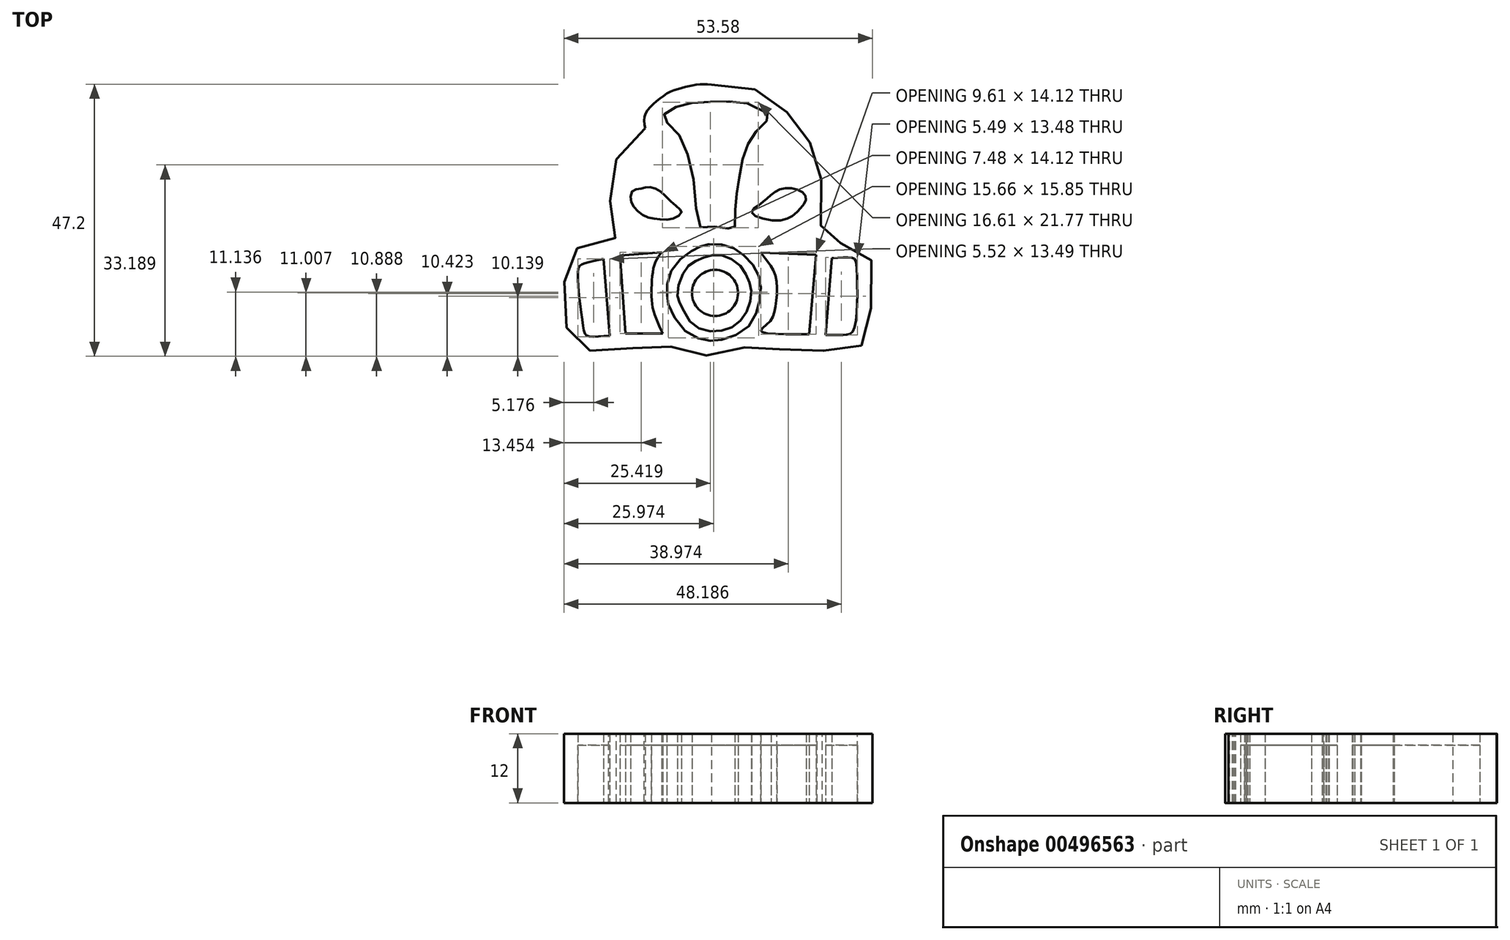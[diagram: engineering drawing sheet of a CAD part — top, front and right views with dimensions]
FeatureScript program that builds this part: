
annotation { "Feature Type Name" : "Feature", "Feature Type Description" : "" }
export const myFeature = defineFeature(function(context is Context, id is Id, definition is map)
    precondition{}
    {
        {
            var Q0;
            Q0=qCreatedBy(makeId("Top.planeOp"),FACE);
            var sketch = newSketch(context, id + "F0", { "sketchPlane" : qUnion([Q0])});
            skFitSpline(sketch, "E0", {"points": [v(28.28, 55.09) * mm, v(31.96, 54.97) * mm, v(34.93, 54.5) * mm, v(37.42, 53.55) * mm, v(40.27, 51.53) * mm, v(41.34, 50.34) * mm, v(41.93, 48.44) * mm, v(43.6, 47.61) * mm, v(45.85, 43.93) * mm, v(46.44, 42.39) * mm, v(47.15, 40.25) * mm, v(47.4, 36.22) * mm, v(47.5, 32.66) * mm, v(47.03, 29.8) * mm, v(46.68, 28.62) * mm, v(48.34, 27.9) * mm, v(51.9, 27.43) * mm, v(54.04, 26.72) * mm, v(55.7, 25.3) * mm, v(56.17, 23.28) * mm, v(56.17, 18.3) * mm, v(55.82, 15.2) * mm, v(55.46, 11.88) * mm, v(54.63, 10.22) * mm, v(52.97, 8.92) * mm, v(49.4, 8.56) * mm, v(47.63, 8.92) * mm, v(43.83, 9.04) * mm, v(40.62, 9.15) * mm, v(38.84, 9.27) * mm, v(35.4, 9.75) * mm, v(34.45, 9.75) * mm, v(32.9, 8.68) * mm, v(29.82, 7.97) * mm, v(27.33, 8.09) * mm, v(24.6, 8.8) * mm, v(23.06, 9.51) * mm, v(20.57, 9.51) * mm, v(18.55, 9.27) * mm, v(16.41, 9.27) * mm, v(13.2, 9.27) * mm, v(11.78, 8.8) * mm, v(7.27, 8.92) * mm, v(5.37, 9.4) * mm, v(3.71, 10.82) * mm, v(3.12, 13.43) * mm, v(3, 17.82) * mm, v(2.76, 20.43) * mm, v(2.76, 23.64) * mm, v(3.6, 25.53) * mm, v(5.37, 26.84) * mm, v(8.93, 27.43) * mm, v(11.19, 27.9) * mm, v(11.78, 29.45) * mm, v(11.43, 31.7) * mm, v(10.83, 34.2) * mm, v(10.48, 37.88) * mm, v(11.43, 40.85) * mm, v(12.02, 42.86) * mm, v(13.92, 45.83) * mm, v(16.77, 47.5) * mm], "startDerivative": vector(190.2, -1.39) * mm, "endDerivative": vector(161.55, 69.83) * mm});
            skFitSpline(sketch, "E1", {"points": [v(16.77, 47.5) * mm, v(16.77, 49.87) * mm, v(18.55, 52) * mm, v(21.04, 53.78) * mm, v(23.53, 54.61) * mm, v(25.79, 55.09) * mm, v(28.28, 55.09) * mm], "startDerivative": vector(-2.45, 15.47) * mm, "endDerivative": vector(15.57, -0.77) * mm});
            skFitSpline(sketch, "E2", {"points": [v(26.38, 30.28) * mm, v(25.43, 36.57) * mm, v(23.65, 44.29) * mm, v(21.4, 47.85) * mm, v(19.73, 49.4) * mm, v(20.68, 50.34) * mm, v(22.94, 51.53) * mm, v(26.62, 52) * mm, v(30.9, 52.12) * mm, v(35.05, 51.65) * mm, v(38.6, 49.4) * mm, v(37.42, 48.56) * mm, v(35.64, 46.3) * mm, v(34.33, 44.17) * mm, v(33.38, 40.6) * mm, v(32.8, 36.93) * mm, v(32.43, 34.32) * mm, v(32.32, 30.52) * mm, v(32.2, 30.04) * mm, v(30.9, 30.16) * mm, v(28.64, 30.4) * mm, v(26.38, 30.28) * mm]});
            skFitSpline(sketch, "E3", {"points": [v(16.05, 37.05) * mm, v(17.24, 37.29) * mm, v(19.02, 36.81) * mm, v(21.16, 34.91) * mm, v(22.82, 33.37) * mm, v(23.06, 32.9) * mm, v(21.63, 31.83) * mm, v(19.02, 31.7) * mm, v(16.89, 32.18) * mm, v(15.1, 33.49) * mm, v(14.27, 35.15) * mm, v(14.63, 36.7) * mm, v(16.05, 37.05) * mm]});
            skCircle(sketch, "E4", {"center": v(28.89, 18.92) * mm, "radius": 4 * mm});
            skPoint(sketch, "E4.first.point", {"position": v(26.38, 15.8) * mm});
            skPoint(sketch, "E4.second.point", {"position": v(31.49, 21.97) * mm});
            skPoint(sketch, "E4.third.point", {"position": v(32.43, 20.79) * mm});
            skFitSpline(sketch, "E5", {"points": [v(20.8, 16.99) * mm, v(20.57, 18.53) * mm, v(20.8, 21.62) * mm, v(23.41, 25.3) * mm, v(26.03, 26.84) * mm, v(27.45, 27.31) * mm, v(30.77, 27.2) * mm, v(33.5, 25.77) * mm, v(35.88, 23.16) * mm, v(36.83, 20.31) * mm, v(36.47, 16.87) * mm, v(34.57, 12.95) * mm, v(30.06, 10.82) * mm, v(27.45, 10.7) * mm, v(23.53, 12.48) * mm, v(20.8, 16.99) * mm]});
            skFitSpline(sketch, "E6", {"points": [v(23.3, 22.21) * mm, v(25.08, 24.23) * mm, v(27.33, 25.18) * mm, v(29.7, 25.53) * mm, v(32.9, 24) * mm, v(34.57, 21.5) * mm, v(35.16, 19.24) * mm, v(34.45, 15.8) * mm, v(32.2, 13.19) * mm, v(28.64, 12.24) * mm, v(24.96, 13.55) * mm, v(22.94, 16.87) * mm, v(22.35, 18.41) * mm, v(23.3, 22.21) * mm]});
            skFitSpline(sketch, "E7", {"points": [v(35.28, 32.9) * mm, v(36.7, 34.32) * mm, v(38.37, 35.74) * mm, v(40.27, 36.93) * mm, v(43, 36.93) * mm, v(44.66, 35.62) * mm, v(44.3, 34.32) * mm, v(42.64, 32.54) * mm, v(39.44, 31.47) * mm, v(35.28, 32.9) * mm]});
            skFitSpline(sketch, "E8", {"points": [v(46.44, 25.53) * mm, v(36.83, 25.9) * mm], "startDerivative": vector(-9.61, 0.36) * mm, "endDerivative": vector(-9.61, 0.36) * mm});
            skFitSpline(sketch, "E9", {"points": [v(36.83, 25.9) * mm, v(37.9, 24.58) * mm, v(39.44, 21.74) * mm, v(39.44, 16.99) * mm, v(38.37, 13.9) * mm, v(36.83, 12.36) * mm, v(45.25, 11.77) * mm], "startDerivative": vector(8.85, -10.47) * mm, "endDerivative": vector(49.24, 0.5) * mm});
            skFitSpline(sketch, "E10", {"points": [v(45.25, 11.77) * mm, v(46.44, 25.53) * mm], "startDerivative": vector(1.19, 13.77) * mm, "endDerivative": vector(1.19, 13.77) * mm});
            skFitSpline(sketch, "E11", {"points": [v(49.17, 24.94) * mm, v(48.1, 11.65) * mm], "startDerivative": vector(-1.07, -13.3) * mm, "endDerivative": vector(-1.07, -13.3) * mm});
            skFitSpline(sketch, "E12", {"points": [v(48.1, 11.65) * mm, v(51.3, 11.65) * mm, v(52.97, 12.6) * mm, v(53.44, 23.52) * mm, v(52.97, 24.94) * mm, v(49.17, 24.94) * mm], "startDerivative": vector(18.48, -0.34) * mm, "endDerivative": vector(-23.5, -2.1) * mm});
            skFitSpline(sketch, "E13", {"points": [v(19.62, 26) * mm, v(12.38, 25.42) * mm], "startDerivative": vector(-7.24, -0.6) * mm, "endDerivative": vector(-7.24, -0.6) * mm});
            skFitSpline(sketch, "E14", {"points": [v(12.38, 25.42) * mm, v(13.32, 11.88) * mm], "startDerivative": vector(0.95, -13.53) * mm, "endDerivative": vector(0.95, -13.53) * mm});
            skFitSpline(sketch, "E15", {"points": [v(13.32, 11.88) * mm, v(19.85, 11.88) * mm], "startDerivative": vector(6.53, 0) * mm, "endDerivative": vector(6.53, 0) * mm});
            skFitSpline(sketch, "E16", {"points": [v(9.53, 24.82) * mm, v(10.6, 11.53) * mm], "startDerivative": vector(1.07, -13.3) * mm, "endDerivative": vector(1.07, -13.3) * mm});
            skFitSpline(sketch, "E17", {"points": [v(10.6, 11.53) * mm, v(6.68, 11.53) * mm, v(5.97, 13.3) * mm, v(5.13, 22.92) * mm, v(5.97, 24) * mm, v(9.53, 24.82) * mm], "startDerivative": vector(-23.18, -2.41) * mm, "endDerivative": vector(20.8, 3.97) * mm});
            skFitSpline(sketch, "E18", {"points": [v(19.62, 26) * mm, v(18.44, 24.04) * mm, v(17.89, 19.89) * mm, v(18.16, 16) * mm, v(19.85, 11.88) * mm], "startDerivative": vector(-6.68, -8.65) * mm, "endDerivative": vector(7.37, -15) * mm});
            skSolve(sketch);
        }
        {
            var Q0;
            Q0=makeQuery(id+"F0.imprint","IMPRINT",FACE,{"disambiguationData":[TD([[makeQuery(id+"F0.imprint","IMPRINT",EDGE,{"derivedFrom":sQuery(id+"F0.wireOp",EDGE,"E4")}),1.0]])]});
            var Q1;
            Q1=makeQuery(id+"F0.imprint","IMPRINT",FACE,{"disambiguationData":[TD([[makeQuery(id+"F0.imprint","IMPRINT",EDGE,{"derivedFrom":sQuery(id+"F0.wireOp",EDGE,"E5")}),-1.0]])]});
            var Q2;
            Q2=makeQuery(id+"F0.imprint","IMPRINT",FACE,{"disambiguationData":[TD([[makeQuery(id+"F0.imprint","IMPRINT",EDGE,{"derivedFrom":sQuery(id+"F0.wireOp",EDGE,"E8")}),1.0]])]});
            var Q3;
            Q3=makeQuery(id+"F0.imprint","IMPRINT",FACE,{"disambiguationData":[TD([[makeQuery(id+"F0.imprint","IMPRINT",EDGE,{"derivedFrom":sQuery(id+"F0.wireOp",EDGE,"E11")}),1.0]])]});
            var Q4;
            Q4=makeQuery(id+"F0.imprint","IMPRINT",FACE,{"disambiguationData":[TD([[makeQuery(id+"F0.imprint","IMPRINT",EDGE,{"derivedFrom":sQuery(id+"F0.wireOp",EDGE,"E16")}),-1.0]])]});
            var Q5;
            Q5=makeQuery(id+"F0.imprint","IMPRINT",FACE,{"disambiguationData":[TD([[makeQuery(id+"F0.imprint","IMPRINT",EDGE,{"derivedFrom":sQuery(id+"F0.wireOp",EDGE,"E13")}),1.0]])]});
            var Q6;
            Q6=makeQuery(id+"F0.imprint","IMPRINT",FACE,{"disambiguationData":[TD([[makeQuery(id+"F0.imprint","IMPRINT",EDGE,{"derivedFrom":sQuery(id+"F0.wireOp",EDGE,"E3")}),-1.0]])]});
            var Q7;
            Q7=makeQuery(id+"F0.imprint","IMPRINT",FACE,{"disambiguationData":[TD([[makeQuery(id+"F0.imprint","IMPRINT",EDGE,{"derivedFrom":sQuery(id+"F0.wireOp",EDGE,"E2")}),-1.0]])]});
            var Q8;
            Q8=makeQuery(id+"F0.imprint","IMPRINT",FACE,{"disambiguationData":[TD([[makeQuery(id+"F0.imprint","IMPRINT",EDGE,{"derivedFrom":sQuery(id+"F0.wireOp",EDGE,"E7")}),-1.0]])]});
            extrude(context, id + "F1", {"entities" : qUnion([Q0, Q1, Q2, Q3, Q4, Q5, Q6, Q7, Q8]), "depth" : 10 * mm, "offsetDistance" : 25 * mm});
        }
        {
            var Q0;
            Q0=makeQuery(id+"F0.imprint","IMPRINT",FACE,{"disambiguationData":[TD([[makeQuery(id+"F0.imprint","IMPRINT",EDGE,{"derivedFrom":sQuery(id+"F0.wireOp",EDGE,"E0")}),-1.0]])]});
            var Q1;
            Q1=makeQuery(id+"F0.imprint","IMPRINT",FACE,{"disambiguationData":[TD([[makeQuery(id+"F0.imprint","IMPRINT",EDGE,{"derivedFrom":sQuery(id+"F0.wireOp",EDGE,"E4")}),-1.0]])]});
            extrude(context, id + "F2", {"entities" : qUnion([Q0, Q1]), "depth" : 12 * mm, "offsetDistance" : 25 * mm});
        }
    });
